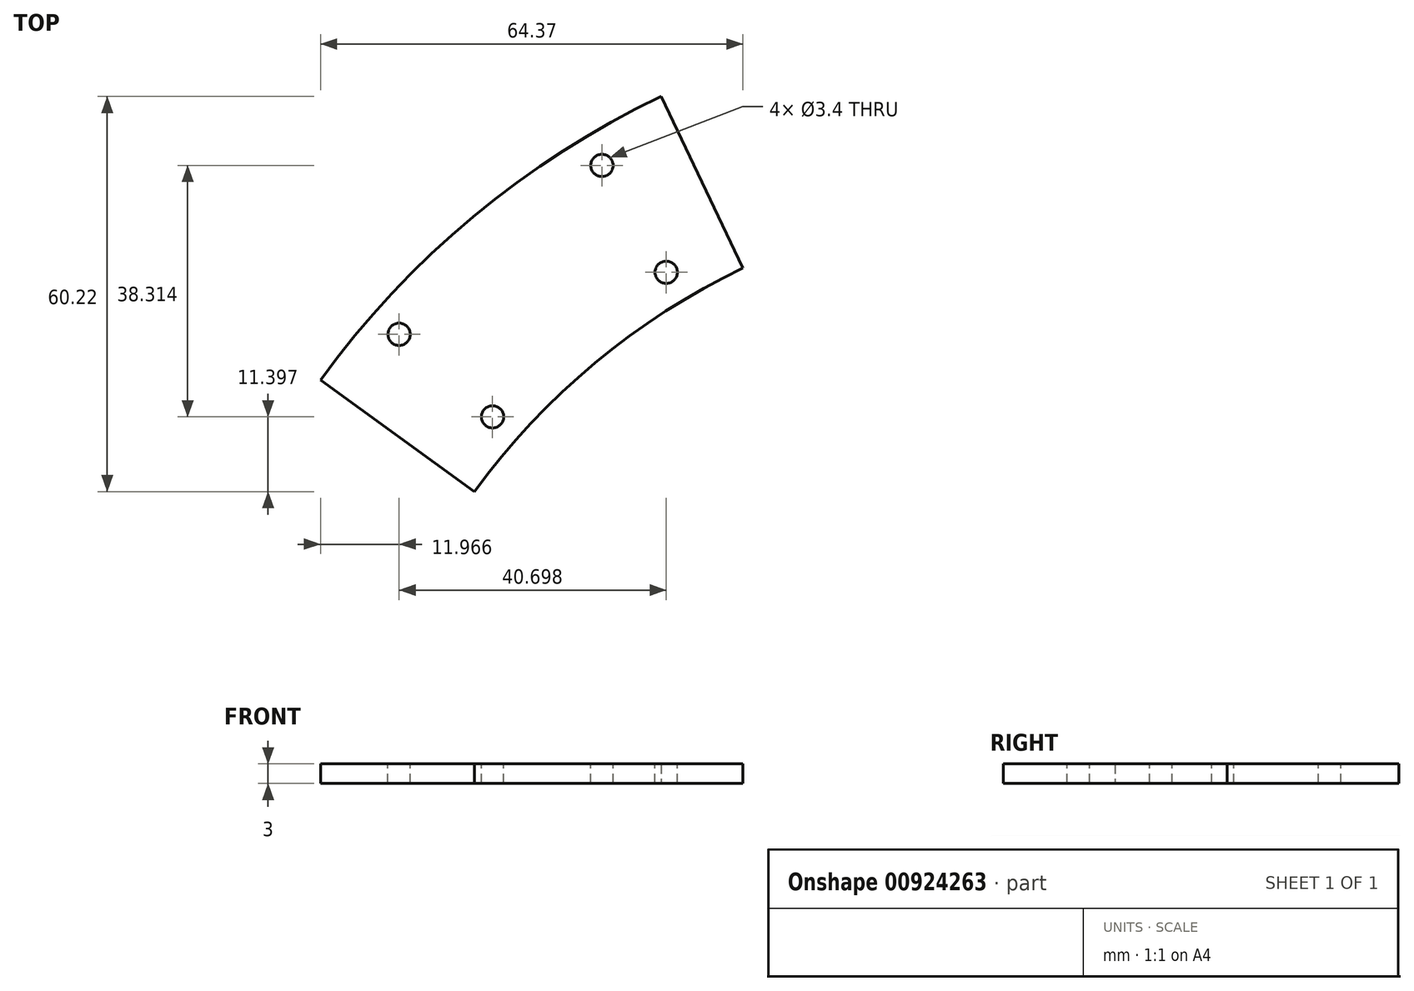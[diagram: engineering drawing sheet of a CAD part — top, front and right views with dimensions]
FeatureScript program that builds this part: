
annotation { "Feature Type Name" : "Feature", "Feature Type Description" : "" }
export const myFeature = defineFeature(function(context is Context, id is Id, definition is map)
    precondition{}
    {
        {
            var Q0;
            Q0=qCreatedBy(makeId("Top.planeOp"),FACE);
            var sketch = newSketch(context, id + "F0", { "sketchPlane" : qUnion([Q0])});
            skLineSegment(sketch, "E0", {"start": v(0, 0) * mm, "end": v(20.27, 186.41) * mm});
            skLineSegment(sketch, "E1", {"start": v(20.27, 186.41) * mm, "end": v(0, 0) * mm});
            skLineSegment(sketch, "E2", {"start": v(151.3, -110.76) * mm, "end": v(0, 0) * mm});
            skLineSegment(sketch, "E3", {"start": v(0, 0) * mm, "end": v(-171.57, -75.65) * mm});
            skCircle(sketch, "E4", {"center": v(0, 0) * mm, "radius": 54 * mm});
            skCircle(sketch, "E5", {"center": v(0, 0) * mm, "radius": 108 * mm});
            skCircle(sketch, "E6", {"center": v(0, 0) * mm, "radius": 140 * mm});
            skLineSegment(sketch, "E7", {"start": v(0, 0) * mm, "end": v(-60.32, 126.34) * mm});
            skLineSegment(sketch, "E8", {"start": v(0, 0) * mm, "end": v(-113.33, 82.2) * mm});
            skLineSegment(sketch, "E9", {"start": v(0, 0) * mm, "end": v(-72.15, 119.98) * mm, "construction": true});
            skLineSegment(sketch, "E10", {"start": v(0, 0) * mm, "end": v(-104.93, 92.68) * mm, "construction": true});
            skPoint(sketch, "E11", {"position": v(-98.93, 87.38) * mm});
            skPoint(sketch, "E12", {"position": v(-84.7, 74.8) * mm});
            skPoint(sketch, "E13", {"position": v(-58.24, 96.84) * mm});
            skPoint(sketch, "E14", {"position": v(-68.03, 113.12) * mm});
            skLineSegment(sketch, "E15", {"start": v(-58.24, 96.84) * mm, "end": v(-55.66, 92.55) * mm});
            skLineSegment(sketch, "E16", {"start": v(-70.6, 117.4) * mm, "end": v(-68.03, 113.12) * mm});
            skLineSegment(sketch, "E17", {"start": v(-102.68, 90.7) * mm, "end": v(-98.93, 87.38) * mm});
            skLineSegment(sketch, "E18", {"start": v(-80.95, 71.5) * mm, "end": v(-84.7, 74.8) * mm});
            skCircle(sketch, "E19", {"center": v(0, 0) * mm, "radius": 137 * mm});
            skCircle(sketch, "E20", {"center": v(-84.7, 74.8) * mm, "radius": 2.8 * mm, "construction": true});
            skCircle(sketch, "E21", {"center": v(-98.93, 87.38) * mm, "radius": 2.8 * mm, "construction": true});
            skLineSegment(sketch, "E22", {"start": v(-86.8, 76.66) * mm, "end": v(-96.84, 85.53) * mm});
            skSolve(sketch);
        }
        {
            var Q0;
            {var subQ1=sQuery(id+"F0.wireOp",EDGE,"E5");var subQ8=makeQuery(id+"F0.imprint","IMPRINT",VERTEX,{"disambiguationData":[OD(0.0)],"derivedFrom":subQ1});Q0=makeQuery(id+"F0.imprint","IMPRINT",FACE,{"disambiguationData":[TD([[makeQuery(id+"F0.imprint","IMPRINT",EDGE,{"disambiguationData":[TD([[subQ8,-1.0]])],"derivedFrom":subQ1}),-1.0]])]});}
            extrude(context, id + "F1", {"entities" : qUnion([Q0]), "depth" : 3 * mm, "offsetDistance" : 25 * mm});
        }
        {
            var Q0;
            Q0=sQuery(id+"F0.wireOp",VERTEX,"E11");
            var Q1;
            Q1=sQuery(id+"F0.wireOp",VERTEX,"E12");
            var Q2;
            Q2=sQuery(id+"F0.wireOp",VERTEX,"E13");
            var Q3;
            Q3=sQuery(id+"F0.wireOp",VERTEX,"E14");
            var Q4;
            Q4=makeQuery(id+"F1.opExtrude","SWEPT_BODY",BODY,{"disambiguationData":[OSD([sQuery(id+"F0.wireOp",EDGE,"E5"),sQuery(id+"F0.wireOp",EDGE,"E7"),sQuery(id+"F0.wireOp",EDGE,"E8"),sQuery(id+"F0.wireOp",EDGE,"E19")])]});
            hole(context, id + "F2", {"style" : HoleStyle.SIMPLE, "endStyle" : HoleEndStyle.THROUGH, "oppositeDirection" : true, "standardTappedOrClearance" : lookupTablePath({ "fit" : "Normal", "standard" : "ISO", "size" : "M3", "type" : "Clearance" }), "standardBlindInLast" : lookupTablePath({ "fit" : "Normal", "standard" : "ISO", "size" : "M3", "type" : "Clearance" }), "holeDiameter" : 3.4 * mm, "majorDiameter" : 5 * mm, "isTappedThrough" : true, "tappedDepth" : 13.5 * mm, "tapClearance" : 3, "locations" : qUnion([Q0, Q1, Q2, Q3]), "scope" : qUnion([Q4]), "startStyle" : HoleStartStyle.PART});
        }
    });
